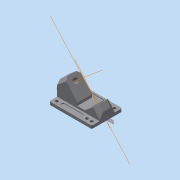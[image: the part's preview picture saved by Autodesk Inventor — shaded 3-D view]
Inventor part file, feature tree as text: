
AUTODESK INVENTOR PART (.ipt)
format: ipt  version: 2014 (Build 180170000, 170)  size: 335,360 bytes
history: native  units: in
note: dims shown in document units (in); Inventor stores cm internally (conversion verified against a paired STEP export)
features: sketch x15, extrude x13, projected_geometry x9, plane x3, chamfer x3, other x3, mirror x1, draft x1, fillet x1
ambient origin geometry x8: Origin, YZ Plane, XZ Plane, XY Plane, X Axis, Y Axis, Z Axis, Center Point
bodies: Solid1 (feature_tree)
feature tree (49):
  extrude  "Extrusion1"  Depth=2.2in
  plane  "Work Plane1"
  extrude  "Extrusion2"  Depth=0.21in TaperAngle=0.0deg
  extrude  "Extrusion3"  Depth=0.205in
  mirror  "Mirror1"
  extrude  "Extrusion4"  Depth=0.278in
  extrude  "Extrusion5"  Depth=0.278in
  extrude  "Extrusion6"  Depth=0.278in
  chamfer  "Chamfer1"  Distance=0.21in
  extrude  "Extrusion7"  Depth=0.3in
  chamfer  "Chamfer2"  Distance=0.05in
  other  "Work Axis1"
  extrude  "Extrusion8"  Depth=0.57in
  extrude  "Extrusion9"  Depth=1.06in
  chamfer  "Chamfer3"  Distance=0.65in
  extrude  "Extrusion10"  Depth=0.3436in
  draft  "FaceDraft5"
  extrude  "Extrusion11"  Depth=0.25in TaperAngle=45.0deg
  sketch  "Sketch14"  dims[d24=0.15in d25=0.0in d26=1.06in d27=0.65in d28=0.0in]
  sketch  "Sketch15"  dims[d34=0.3436in d35=0.3436in]
  extrude  "Extrusion13"  Depth=0.5in
  fillet  "Fillet2"  Radius=0.5in
  other  "Work Axis2"
  extrude  "Extrusion14"  Depth=0.25in TaperAngle=45.0deg
  plane  "Work Plane4"
  sketch  "Sketch18"  dims[d41=0.7in d42=0.5in d43=0.5in d44=0.0in d46=0.25in d47=0.125in d48=45.0deg d49=1.46in d50=1.3in d51=0.0in d52=0.2in d53=0.3436in d54=0.3436in d55=1.3in d56=0.0in d57=0.2in d58=0.125in d59=45.0deg d63=0.66in d64=0.125in d65=0.4in d66=0.0in d67=0.3436in d68=0.37in d69=0.4in d70=0.0in d71=1.1in d72=0.76in d73=0.0in d74=0.11in d75=0.8in d76=0.8933in d77=90.0deg d78=0.4in d79=0.4in d82=0.76in d83=0.0in d84=0.135in d85=1.08in d86=0.75in d87=0.05in d88=0.05in d89=0.5in d90=0.03in d91=0.0in d92=0.0137in]
  other  "Work Axis3"
  sketch  "Sketch1"  dims[d0=3.074in d1=2.2in]
  sketch  "Sketch2"  dims[d2=0.1in d3=0.21in d4=0.0in]
  sketch  "Sketch3"  dims[d5=0.205in d6=0.205in]
  plane  "Work Plane2"
  sketch  "Sketch4"  dims[d7=0.205in d8=0.278in]
  projected_geometry  "Projected Loop1"
  sketch  "Sketch5"  dims[d9=0.278in d10=0.278in]
  projected_geometry  "Projected Loop2"
  sketch  "Sketch8"  dims[d11=0.278in d12=0.278in]
  projected_geometry  "Projected Loop4"
  sketch  "Sketch9"  dims[d13=0.35in d14=0.21in d15=0.0in]
  sketch  "Sketch10"  dims[d16=0.3in d17=0.45in]
  projected_geometry  "Projected Loop5"
  sketch  "Sketch11"  dims[d18=0.45in]
  projected_geometry  "Projected Loop6"
  sketch  "Sketch12"  dims[d19=0.0in d20=0.05in d21=0.0in]
  projected_geometry  "Projected Loop7"
  sketch  "Sketch13"  dims[d22=0.57in d23=0.57in]
  projected_geometry  "Projected Loop8"
  projected_geometry  "Projected Loop9"
  projected_geometry  "Projected Loop10"
  sketch  "Sketch17"  dims[d36=0.75in d37=0.0in d38=0.25in d39=0.125in d40=45.0deg]
